# Revit family: SHR450-SER450
name_source: partatom
category: Mechanical Equipment
revit_build: Autodesk Revit 2016 (Build: 20170117_1200(x64)
units: mm (PartAtom-declared; Revit-internal decimal feet)

## family parameters
Always vertical = Yes
Cut with Voids When Loaded = No
OmniClass Number = 23.75.00.00
OmniClass Title = Climate Control (HVAC)
Part Type = Normal
Room Calculation Point = No
Round Connector Dimension = Use Diameter
Shared = No
Work Plane-Based = No

## types (3) — shared parameters
Load Classification = HVAC
Manufacturer = Fantech
Power Factor = 1
URL = http://www.fantech.net
Voltage = 120 V

## per-type parameters (varying)
| type | Airflow | BPM | Current | Description | Model | Power Rated | Product number | Weight | construction | under bpm |
| SER 450 | 468 cfm | No | 4.17 A | Light Commercial Energy Recovery Ventilators | SER 450 | 500 W | 99266 | 132 lbs | 2 | Yes |
| SHR 450 | 465 cfm | No | 3.92 A | Commercial Heat Recovery Ventilators | SHR 450 | 470 W | 99210 | 146 lbs | 2 | Yes |
| SHR 450 BPM | 465 cfm | Yes | 3.92 A | Commercial Heat Recovery Ventilators | SHR 450 | 470 W | 99210, 99300 | 146 lbs | 99 | No |

## geometry (parser evidence)
native form markers: Blend x2, Sweep x3
no freeform markers — native parametric forms only
